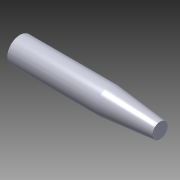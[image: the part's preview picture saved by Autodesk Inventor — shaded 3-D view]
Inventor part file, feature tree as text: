
AUTODESK INVENTOR PART (.ipt)
format: ipt  version: 2015 (Build 190159000, 159)  size: 108,544 bytes
history: native  units: in
note: dims shown in document units (in); Inventor stores cm internally (conversion verified against a paired STEP export)
features: revolve x1, other x1, imported_body x1
ambient origin geometry x8: Origin, YZ Plane, XZ Plane, XY Plane, X Axis, Y Axis, Z Axis, Center Point
bodies: Body1 (feature_tree)
feature tree (3):
  revolve  "Revolve1"  [1 undecoded]
  other  "Platen1"
  imported_body  "Base1"
note: 1 required parameter value undecoded (feature->parameter linkage not recoverable at this tier; creation-order binding heuristic only, values carry confidence <= 0.55)
